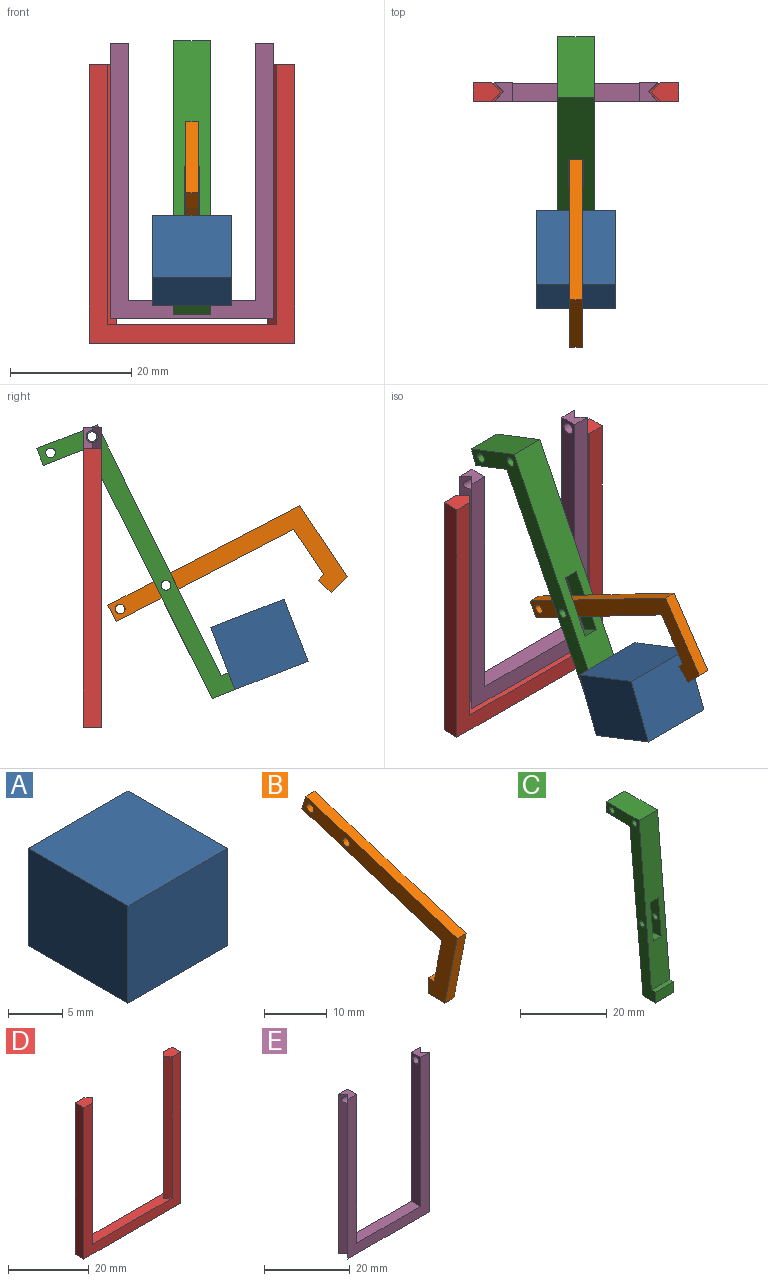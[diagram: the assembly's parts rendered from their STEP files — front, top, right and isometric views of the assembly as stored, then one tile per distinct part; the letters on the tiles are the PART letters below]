
ASSEMBLY  parts=5 mates=4
PART A: 6 faces, bbox 13x13x11 mm
  f0: plane 13x11mm, normal (0,1,0), area 143mm2, adj f1,f3,f4,f5
  f1: plane 13x11mm, normal (-1,0,0), area 143mm2, adj f0,f2,f4,f5
  f2: plane 13x11mm, normal (0,-1,0), area 143mm2, adj f1,f3,f4,f5
  f3: plane 13x11mm, normal (1,0,0), area 143mm2, adj f0,f2,f4,f5
  f4: plane 13x13mm, normal (0,0,1), area 169mm2, adj f0,f1,f2,f3
  f5: plane 13x13mm, normal (0,0,-1), area 169mm2, adj f0,f1,f2,f3
PART B: 12 faces, bbox 2x34.9x24.6 mm
  f0: plane 31.46x9.97mm, normal (0,0.3,-0.95), area 66mm2, adj f1,f8,f10,f11
  f1: plane 2.86x2mm, normal (0,0.95,0.3), area 6mm2, adj f0,f2,f10,f11
  f2: plane 34x10.77mm, normal (0,-0.3,0.95), area 71.3mm2, adj f1,f3,f10,f11
  f3: plane 13.87x2.74mm, normal (0,-0.98,-0.19), area 28.3mm2, adj f2,f4,f10,f11
  f4: plane 3.74x2mm, normal (0,0,-1), area 7.5mm2, adj f3,f5,f10,f11
  f5: plane 3x2mm, normal (0,1,0), area 6mm2, adj f4,f6,f10,f11
  f6: plane 2x1.3mm, normal (0,0,1), area 2.6mm2, adj f5,f8,f10,f11
  f7: cylinder r=0.8mm len=2mm, axis (-1,0,0), area 10.1mm2, adj f10,f11
  f8: plane 8.82x2mm, normal (0,0.98,0.19), area 18mm2, adj f0,f6,f10,f11
  f9: cylinder r=0.8mm len=2mm, axis (-1,0,0), area 10.1mm2, adj f10,f11
  f10: plane 34.9x24.64mm, normal (1,0,0), area 141mm2, adj f0,f1,f2,f3,f4,f5,f6,f7
  f11: plane 34.9x24.64mm, normal (-1,0,0), area 141mm2, adj f0,f1,f2,f3,f4,f5,f6,f7
PART C: 18 faces, bbox 6x16x49 mm
  f0: cylinder r=0.8mm len=1.7mm, axis (-1,0,0), area 8.5mm2, adj f13,f17
  f1: plane 10.72x6mm, normal (0,0,1), area 64.3mm2, adj f2,f8,f12,f13
  f2: plane 46x6mm, normal (0,-1,0.09), area 249.6mm2, adj f1,f3,f12,f13,f14,f15,f16,f17
  f3: plane 6x1.3mm, normal (0,0,1), area 7.8mm2, adj f2,f4,f12,f13
  f4: plane 6x3mm, normal (0,-1,0), area 18mm2, adj f3,f5,f12,f13
  f5: plane 6x4.04mm, normal (0,0,-1), area 24.2mm2, adj f4,f6,f12,f13
  f6: plane 46x6mm, normal (0,1,-0.09), area 249.8mm2, adj f5,f7,f12,f13,f14,f15,f16,f17
  f7: plane 7.72x6mm, normal (0,0,-1), area 46.3mm2, adj f6,f8,f12,f13
  f8: plane 6x3mm, normal (0,1,0), area 18mm2, adj f1,f7,f12,f13
  f9: cylinder r=0.8mm len=6mm, axis (-1,0,0), area 30.2mm2, adj f12,f13
  f10: cylinder r=0.8mm len=6mm, axis (-1,0,0), area 30.2mm2, adj f12,f13
  f11: cylinder r=0.8mm len=1.7mm, axis (-1,0,0), area 8.5mm2, adj f12,f16
  f12: plane 49x16.04mm, normal (1,0,0), area 174.1mm2, adj f1,f2,f3,f4,f5,f6,f7,f8
  f13: plane 49x16.04mm, normal (-1,0,0), area 174.1mm2, adj f0,f1,f2,f3,f4,f5,f6,f7
  f14: plane 3.06x2.6mm, normal (0,0.09,1), area 8mm2, adj f2,f6,f16,f17
  f15: plane 3.12x2.6mm, normal (0,-0.09,-1), area 8.2mm2, adj f2,f6,f16,f17
  f16: plane 10.78x4.04mm, normal (-1,0,0), area 30.7mm2, adj f2,f6,f11,f14,f15
  f17: plane 10.78x4.04mm, normal (1,0,0), area 30.7mm2, adj f0,f2,f6,f14,f15
PART D: 12 faces, bbox 34x3x46 mm
  f0: plane 28x3mm, normal (0,0,1), area 79.5mm2, adj f6,f7,f8,f9,f10,f11
  f1: plane 46x3mm, normal (1,0,0), area 138mm2, adj f2,f5,f6,f7
  f2: plane 4.5x3mm, normal (0,0,1), area 11.3mm2, adj f1,f6,f7,f10,f11
  f3: plane 4.5x3mm, normal (0,0,1), area 11.3mm2, adj f4,f6,f7,f8,f9
  f4: plane 46x3mm, normal (-1,0,0), area 138mm2, adj f3,f5,f6,f7
  f5: plane 34x3mm, normal (0,0,-1), area 102mm2, adj f1,f4,f6,f7
  f6: plane 46x34mm, normal (0,-1,0), area 360mm2, adj f0,f1,f2,f3,f4,f5,f9,f11
  f7: plane 46x34mm, normal (0,1,0), area 360mm2, adj f0,f1,f2,f3,f4,f5,f8,f10
  f8: plane 43x1.5mm, normal (0.71,0.71,0), area 91.2mm2, adj f0,f3,f7,f9
  f9: plane 43x1.5mm, normal (0.71,-0.71,0), area 91.2mm2, adj f0,f3,f6,f8
  f10: plane 43x1.5mm, normal (-0.71,0.71,0), area 91.2mm2, adj f0,f2,f7,f11
  f11: plane 43x1.5mm, normal (-0.71,-0.71,0), area 91.2mm2, adj f0,f2,f6,f10
PART E: 14 faces, bbox 27x3x45.5 mm
  f0: plane 3x3mm, normal (0,0,1), area 6.7mm2, adj f4,f6,f7,f10,f11
  f1: plane 27x3mm, normal (0,0,-1), area 76.5mm2, adj f6,f7,f8,f9,f10,f11
  f2: plane 42.47x3mm, normal (-1,0,0), area 124.3mm2, adj f3,f5,f6,f7,f13
  f3: plane 21x3mm, normal (0,0,1), area 63mm2, adj f2,f4,f6,f7
  f4: plane 42.47x3mm, normal (1,0,0), area 124.3mm2, adj f0,f3,f6,f7,f12
  f5: plane 3x3mm, normal (0,0,1), area 6.7mm2, adj f2,f6,f7,f8,f9
  f6: plane 45.47x27mm, normal (0,-1,0), area 335.8mm2, adj f0,f1,f2,f3,f4,f5,f9,f11
  f7: plane 45.47x27mm, normal (0,1,0), area 335.8mm2, adj f0,f1,f2,f3,f4,f5,f8,f10
  f8: plane 45.47x1.5mm, normal (0.71,-0.71,0), area 94.2mm2, adj f1,f5,f7,f9,f13
  f9: plane 45.47x1.5mm, normal (0.71,0.71,0), area 94.2mm2, adj f1,f5,f6,f8,f13
  f10: plane 45.47x1.5mm, normal (-0.71,-0.71,0), area 94.2mm2, adj f0,f1,f7,f11,f12
  f11: plane 45.47x1.5mm, normal (-0.71,0.71,0), area 94.2mm2, adj f0,f1,f6,f10,f12
  f12: cylinder r=1mm len=2.5mm, axis (1,0,0), area 13.4mm2, adj f4,f10,f11
  f13: cylinder r=1mm len=2.5mm, axis (1,0,0), area 13.4mm2, adj f2,f8,f9
PLACE A rot(axis=(-1,0,0),21.3deg) t=(-7.47,-1.55,-7.75)mm
PLACE B rot(axis=(-1,0,0),45deg) t=(-7.47,-10.05,-4.32)mm
PLACE C rot(axis=(-1,0,0),21.3deg) t=(-7.47,-2.21,-7.49)mm
PLACE D t=(-7.47,15.13,-10.66)mm fixed
PLACE E t=(-7.47,15.13,-10.19)mm
MATE fastened A.f0 <-> C.f4  axis (0,0.93,-0.36) through (-7.47,-9.96,-4.48)mm
MATE slider E.f1 <-> D.f0  axis (0,0,1) through (-7.47,13.63,-6.66)mm
MATE revolute E.f12 <-> C.f10  axis (1,0,0) through (-17.97,13.63,37.31)mm
MATE revolute C.f0 <-> B.f7  axis (-1,0,0) through (-6.17,1.43,12.75)mm
